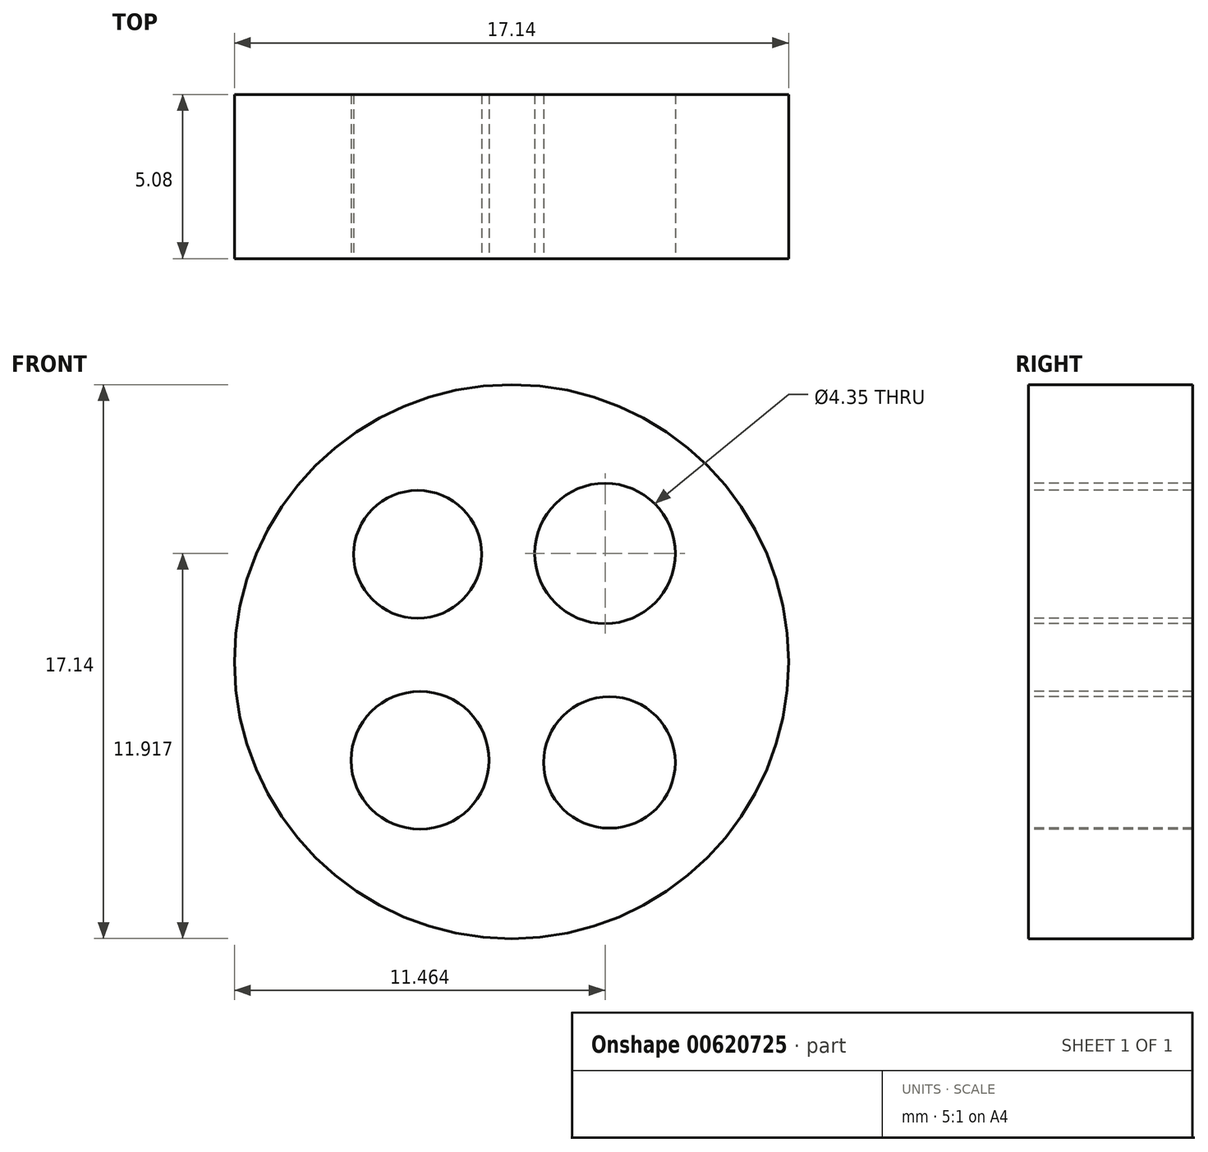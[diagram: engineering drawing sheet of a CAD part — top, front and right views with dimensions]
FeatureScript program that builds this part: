
annotation { "Feature Type Name" : "Feature", "Feature Type Description" : "" }
export const myFeature = defineFeature(function(context is Context, id is Id, definition is map)
    precondition{}
    {
        {
            var Q0;
            Q0=qCreatedBy(makeId("Front.planeOp"),FACE);
            var sketch = newSketch(context, id + "F0", { "sketchPlane" : qUnion([Q0])});
            skCircle(sketch, "E0", {"center": v(0, 0) * mm, "radius": 8.57 * mm});
            skSolve(sketch);
        }
        {
            var Q0;
            Q0 = qSketchRegion(id + "F0", true);
            extrude(context, id + "F1", {"entities" : qUnion([Q0]), "depth" : 5.08 * mm, "offsetDistance" : 25.4 * mm});
        }
        {
            var Q0;
            Q0=makeQuery(id+"F1.opExtrude","CAP_FACE",FACE,{"disambiguationData":[OSD([sQuery(id+"F0.wireOp",EDGE,"E0")])],"isStart":false});
            var sketch = newSketch(context, id + "F2", { "sketchPlane" : qUnion([Q0])});
            skCircle(sketch, "E1", {"center": v(-2.9, 3.32) * mm, "radius": 1.98 * mm});
            skCircle(sketch, "E2", {"center": v(2.9, 3.35) * mm, "radius": 2.17 * mm});
            skCircle(sketch, "E3", {"center": v(3.03, -3.12) * mm, "radius": 2.04 * mm});
            skCircle(sketch, "E4", {"center": v(-2.83, -3.05) * mm, "radius": 2.13 * mm});
            skSolve(sketch);
        }
        {
            var Q0;
            Q0 = qSketchRegion(id + "F2", true);
            extrude(context, id + "F3", {"entities" : qUnion([Q0]), "operationType" : NewBodyOperationType.REMOVE, "oppositeDirection" : true, "depth" : 25.4 * mm, "offsetDistance" : 25.4 * mm});
        }
    });
